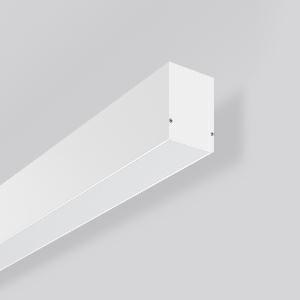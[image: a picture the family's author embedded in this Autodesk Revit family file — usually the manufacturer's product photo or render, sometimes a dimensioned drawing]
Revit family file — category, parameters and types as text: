
# Revit family: less_is_more_50_312605_002_76_b2a3
name_source: partatom
category: Lighting Fixtures
units: mm (PartAtom-declared; Revit-internal decimal feet)

## family parameters
Cut with Voids When Loaded = No
Host = Face
Light Source = No
Part Type = Normal
Room Calculation Point = No
Round Connector Dimension = Use Diameter
Shared = No

## types (1)
- LESS IS MORE 50 (1 x LED Modul 830, 1100 lm, 3000)
    Apparent Load = 9 VA
    CIE Flux Codes = 48 80 96 100 100
    Color Rendering = 80
    Color Temperature = 3000
    Default Elevation = 1800 mm
    Description = Series: LESS IS MORE 50
Linear wall luminaires. Housing: extruded aluminium profile, powder-coated. End cap aluminium powder-coated. Diffuser made of non-yellowing plastic (PMMA), opal. Direct light emission. Suitable for Wall (surface). LED unit with integrated converter interchangeable and removable. Suitable for through-wiring. With sensors or as a safety luminaire on request. 
Colour: traffic white, matt (RAL 9016)
Length: 847 mm
Width: 67 mm
Height: 75 mm
Lamp: LED
Socket: without socket
Colour temperature: 3000K
Colour rendering index (CRI): 80
System power: 9 W
Rated luminous flux: 1100 lm
Luminous efficiency: 122 lm/W
Control gear: Converter, dimmable, DALI
Protection class: I
Type of protection: IP 20
    Height = 75 mm
    Lamp = 1 x LED Modul 830
    Lamp Light Flux = 1100 lm
    Lamp count = 1
    Length = 847 mm
    Lifetime = 50000 h
    Luminous efficacy = 122 lm/W
    Manufacturer = RZB
    ModVariant = No
    Model = 312605.002.76
    Mounting Place = Wall
    Mounting Type = Surface mounted
    Number of Poles = 1
    OnlyDefault = Yes
    Power Factor = 1
    Product Name = LESS IS MORE 50
    Product group = Surface mounted LED linear luminaires
    ProductGroupID = 2007
    Protection Class = Protection class I
    Protection Degree = IP 20
    RLX_Detail_Level = 1
    RLX_Emergency_Light_Flux = 0 lm
    RLX_Emergency_Type = 0
    RLX_Emergency_Type_DB = No
    RlxData = <blob elided: 35165 chars, md5=156944df>
    Socket = socket
    Standby Power = 0 W
    System Light Flux = 1100 lm
    System Power = 9 W
    Type Comments = Product without accessories
    Type Image = 312606.002.jpg
    URL = http://relux.com
    VarID = ---
    Voltage = 0 V
    Weight = 0.00 kg
    Width = 67 mm

## geometry (parser evidence)
native form markers: Blend x4, Sweep x11
no freeform markers — native parametric forms only
